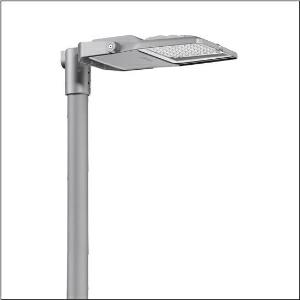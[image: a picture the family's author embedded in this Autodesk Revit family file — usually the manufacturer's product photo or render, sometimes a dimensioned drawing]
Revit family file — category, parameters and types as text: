
# Revit family: floodlight_fl_21_mini___pl64_5xa7775c2e3a_8880
name_source: partatom
category: Lighting Fixtures
units: mm (PartAtom-declared; Revit-internal decimal feet)

## family parameters
Cut with Voids When Loaded = No
Host = Face
Light Source = No
Part Type = Normal
Room Calculation Point = No
Round Connector Dimension = Use Diameter
Shared = No

## types (1)
- --- (1 x LED, 11770 lm, 89 W, 3000K)
    Apparent Load = 89 VA
    CIE Flux Codes = 28 80 98 100 100
    Color Rendering = 70
    Color Temperature = 3000K
    Default Elevation = 1800 mm
    Description = Floodlight FL 21 mini, floodlight, primary light control with lens, of PMMA, primary optical cover: protective disc, of toughened safety glass, transparent, light distribution: PL64, light emission: direct distribution, installation type: surface-mounted, LED, High Power LED, rated luminous flux: 11.770lm, luminous efficacy: 132lm/W, light colour: 730, colour temperature: 3000K, control: flexible luminous flux parameterisation, time-dependent luminous flux control, constant luminous flux control, overheat protection, presetting dimming logarithmic, with terminal, 6-pole, mains connection: 220..240V, AC, 50/60Hz, start of lifetime: 89W, end of service life: 94W, reduction: 43W, luminaire housing, of diecast aluminium, powder-coated, Siteco® metallic grey (DB 702S), corrosivity category C5 mid according to DIN EN ISO 12944, sealing non-destructively replaceable, please order mast flange separately, mast bracket, of steel, galvanised, powder-coated, Siteco® metallic grey (DB 702S), Smart Interface above, protection rating (complete): IP66, insulation class (complete): insulation class II (safety insulation), certification: CE, ENEC, VDE, protection symbol: D, impact resistance: IK08, permissible operating ambient temperature: -40..+40°C, permissible operating ambient temperature for outdoor applications: -40..+50°C, standard: DIN EN 12944, LABS conformity tested according to VDMA 24364:2018-05, packaging unit: 1 piece

Light Distribution: PL64
    Height = 70 mm
    Lamp = 1 x LED
    Lamp Light Flux = 11770 lm
    Lamp Power = 89 W
    Lamp count = 1
    Length = 485 mm
    Luminous efficacy = 132 lm/W
    Manufacturer = Siteco
    ModVariant = No
    Model = 5XA7775C2E3A
    Number of Poles = 1
    OnlyDefault = Yes
    Power Factor = 1
    Product Name = Floodlight FL 21 mini | PL64
    Product group = floodlight | pylon annexe
    ProductGroupID = 6200
    Protection Class = Protection class II
    Protection Degree = IP 66
    RLX_Detail_Level = 1
    RLX_Emergency_Light_Flux = 0 lm
    RLX_Emergency_Type = 0
    RLX_Emergency_Type_DB = No
    RlxData = <blob elided: 100973 chars, md5=b7444e7e>
    Socket = socket
    Standby Power = 0 W
    System Light Flux = 11770 lm
    System Power = 89 W
    Type Comments = factory setting: luminous flux: 100 % | dim-lin: 254 | 456 mA
    Type Image = l_1007125.jpg
    URL = http://relux.com
    VarID = @adj_115563
    Voltage = 0 V
    Weight = 0.00 kg
    Width = 337 mm

## geometry (parser evidence)
native form markers: Blend x4, Sweep x12
no freeform markers — native parametric forms only
